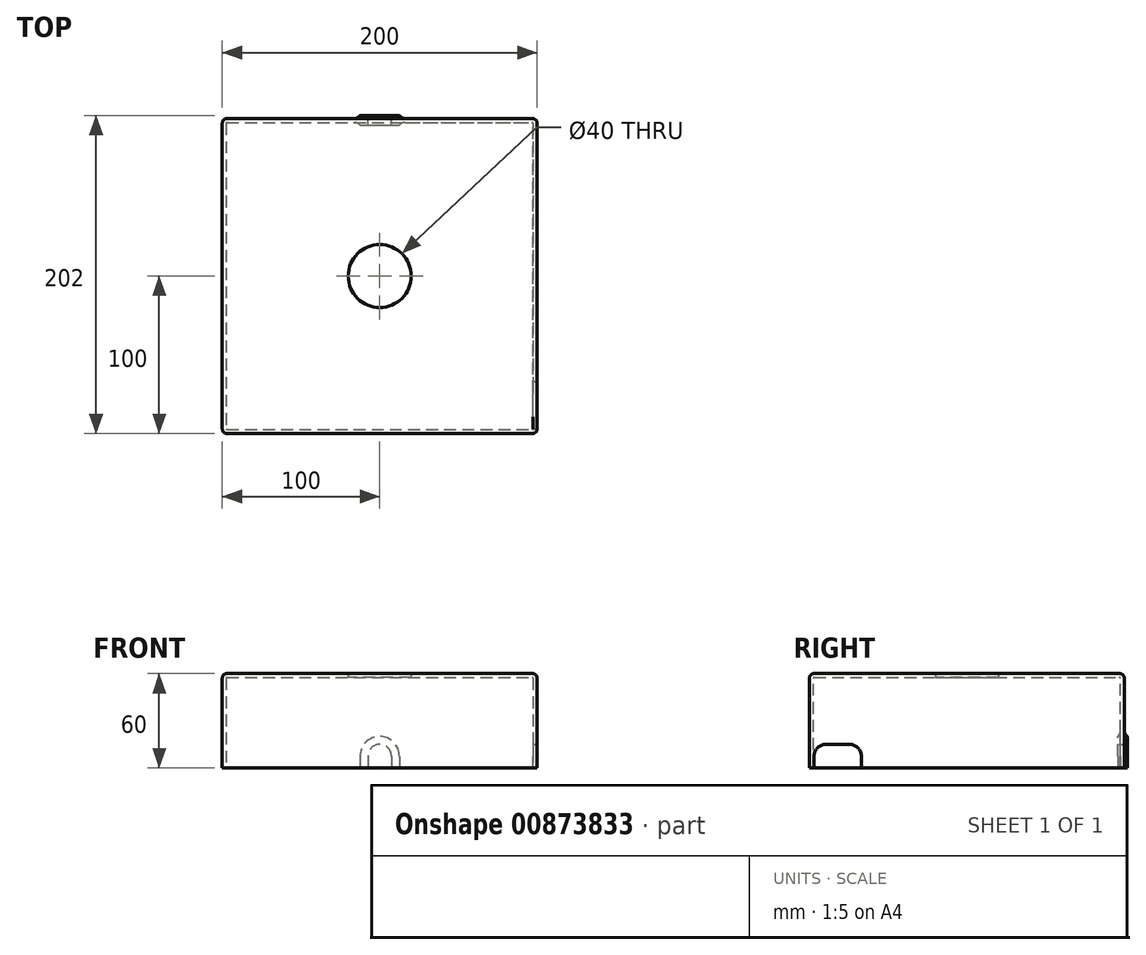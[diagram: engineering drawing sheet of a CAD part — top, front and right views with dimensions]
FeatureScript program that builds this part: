
annotation { "Feature Type Name" : "Feature", "Feature Type Description" : "" }
export const myFeature = defineFeature(function(context is Context, id is Id, definition is map)
    precondition{}
    {
        {
            var Q0;
            Q0=qCreatedBy(makeId("Top.planeOp"),FACE);
            var sketch = newSketch(context, id + "F0", { "sketchPlane" : qUnion([Q0])});
            skLineSegment(sketch, "E0.bottom", {"start": v(0, 0) * mm, "end": v(200, 0) * mm});
            skLineSegment(sketch, "E0.top", {"start": v(0, -200) * mm, "end": v(200, -200) * mm});
            skLineSegment(sketch, "E0.left", {"start": v(0, 0) * mm, "end": v(0, -200) * mm});
            skLineSegment(sketch, "E0.right", {"start": v(200, 0) * mm, "end": v(200, -200) * mm});
            skCircle(sketch, "E1", {"center": v(100, -100) * mm, "radius": 20 * mm});
            skPoint(sketch, "E1.centerSnap0", {"position": v(0, -100) * mm});
            skPoint(sketch, "E1.centerSnap1", {"position": v(100, 0) * mm});
            skSolve(sketch);
        }
        {
            var Q0;
            Q0=makeQuery(id+"F0.imprint","IMPRINT",FACE,{"disambiguationData":[TD([[makeQuery(id+"F0.imprint","IMPRINT",EDGE,{"derivedFrom":sQuery(id+"F0.wireOp",EDGE,"E0.bottom")}),-1.0]])]});
            var Q1;
            Q1=makeQuery(id+"F0.imprint","IMPRINT",FACE,{"disambiguationData":[TD([[makeQuery(id+"F0.imprint","IMPRINT",EDGE,{"derivedFrom":sQuery(id+"F0.wireOp",EDGE,"E1")}),1.0]])]});
            extrude(context, id + "F1", {"entities" : qUnion([Q0, Q1]), "depth" : 60 * mm, "offsetDistance" : 25 * mm});
        }
        {
            var Q0;
            Q0=makeQuery(id+"F1.opExtrude","CAP_EDGE",EDGE,{"disambiguationData":[OSD([sQuery(id+"F0.wireOp",EDGE,"E0.bottom")])],"isStart":false});
            var Q1;
            Q1=makeQuery(id+"F1.opExtrude","CAP_EDGE",EDGE,{"disambiguationData":[OSD([sQuery(id+"F0.wireOp",EDGE,"E0.right")])],"isStart":false});
            var Q2;
            Q2=makeQuery(id+"F1.opExtrude","CAP_EDGE",EDGE,{"disambiguationData":[OSD([sQuery(id+"F0.wireOp",EDGE,"E0.top")])],"isStart":false});
            var Q3;
            Q3=makeQuery(id+"F1.opExtrude","CAP_EDGE",EDGE,{"disambiguationData":[OSD([sQuery(id+"F0.wireOp",EDGE,"E0.left")])],"isStart":false});
            var Q4;
            Q4=makeQuery(id+"F1.opExtrude","SWEPT_EDGE",EDGE,{"disambiguationData":[OSD([sQuery(id+"F0.wireOp",EDGE,"E0.bottom"),sQuery(id+"F0.wireOp",EDGE,"E0.left")])]});
            var Q5;
            Q5=makeQuery(id+"F1.opExtrude","SWEPT_EDGE",EDGE,{"disambiguationData":[OSD([sQuery(id+"F0.wireOp",EDGE,"E0.top"),sQuery(id+"F0.wireOp",EDGE,"E0.left")])]});
            var Q6;
            Q6=makeQuery(id+"F1.opExtrude","SWEPT_EDGE",EDGE,{"disambiguationData":[OSD([sQuery(id+"F0.wireOp",EDGE,"E0.top"),sQuery(id+"F0.wireOp",EDGE,"E0.right")])]});
            var Q7;
            Q7=makeQuery(id+"F1.opExtrude","SWEPT_EDGE",EDGE,{"disambiguationData":[OSD([sQuery(id+"F0.wireOp",EDGE,"E0.bottom"),sQuery(id+"F0.wireOp",EDGE,"E0.right")])]});
            fillet(context, id + "F2", {"entities" : qUnion([Q0, Q1, Q2, Q3, Q4, Q5, Q6, Q7]), "radius" : 3 * mm, "tangentPropagation" : true, "allowEdgeOverflow" : false});
        }
        {
            var Q0;
            Q0=makeQuery(id+"F1.opExtrude","CAP_FACE",FACE,{"disambiguationData":[OSD([sQuery(id+"F0.wireOp",EDGE,"E0.bottom"),sQuery(id+"F0.wireOp",EDGE,"E0.top"),sQuery(id+"F0.wireOp",EDGE,"E0.left"),sQuery(id+"F0.wireOp",EDGE,"E0.right")])],"isStart":true});
            shell(context, id + "F3", {"entities" : qUnion([Q0]), "thickness" : 2.5 * mm});
        }
        {
            var Q0;
            Q0=makeQuery(id+"F0.imprint","IMPRINT",FACE,{"disambiguationData":[TD([[makeQuery(id+"F0.imprint","IMPRINT",EDGE,{"derivedFrom":sQuery(id+"F0.wireOp",EDGE,"E1")}),1.0]])]});
            var Q1;
            Q1=makeQuery(id+"F1.opExtrude","CAP_FACE",FACE,{"disambiguationData":[OSD([sQuery(id+"F0.wireOp",EDGE,"E0.bottom"),sQuery(id+"F0.wireOp",EDGE,"E0.top"),sQuery(id+"F0.wireOp",EDGE,"E0.left"),sQuery(id+"F0.wireOp",EDGE,"E0.right")])],"isStart":false});
            extrude(context, id + "F4", {"entities" : qUnion([Q0]), "operationType" : NewBodyOperationType.REMOVE, "endBound" : BoundingType.UP_TO_SURFACE, "depth" : 25 * mm, "endBoundEntityFace" : qUnion([Q1]), "offsetDistance" : 25 * mm});
        }
        {
            var Q0;
            Q0=makeQuery(id+"F1.opExtrude","SWEPT_FACE",FACE,{"disambiguationData":[OSD([sQuery(id+"F0.wireOp",EDGE,"E0.right")])]});
            var sketch = newSketch(context, id + "F5", { "sketchPlane" : qUnion([Q0])});
            skLineSegment(sketch, "E2.bottom", {"start": v(-197, 0) * mm, "end": v(-167, 0) * mm});
            skLineSegment(sketch, "E2.top", {"start": v(-189.5, 15) * mm, "end": v(-174.5, 15) * mm});
            skLineSegment(sketch, "E2.left", {"start": v(-197, 0) * mm, "end": v(-197, 7.5) * mm});
            skLineSegment(sketch, "E2.right", {"start": v(-167, 0) * mm, "end": v(-167, 7.5) * mm});
            skPoint(sketch, "E3.visualSharp", {"position": v(-197, 15) * mm});
            skArc(sketch, "E3.filletArc", {"start": v(-189.5, 15) * mm, "mid": v(-194.8, 12.8) * mm, "end": v(-197, 7.5) * mm});
            skPoint(sketch, "E4.visualSharp", {"position": v(-167, 15) * mm});
            skArc(sketch, "E4.filletArc", {"start": v(-167, 7.5) * mm, "mid": v(-169.2, 12.8) * mm, "end": v(-174.5, 15) * mm});
            skSolve(sketch);
        }
        {
            var Q0;
            Q0=makeQuery(id+"F5.imprint","IMPRINT",FACE,{"disambiguationData":[TD([[makeQuery(id+"F5.imprint","IMPRINT",EDGE,{"derivedFrom":sQuery(id+"F5.wireOp",EDGE,"E2.bottom")}),-1.0]])]});
            extrude(context, id + "F6", {"entities" : qUnion([Q0]), "operationType" : NewBodyOperationType.REMOVE, "oppositeDirection" : true, "depth" : 25 * mm, "offsetDistance" : 25 * mm});
        }
        {
            var Q0;
            Q0=makeQuery(id+"F1.opExtrude","SWEPT_FACE",FACE,{"disambiguationData":[OSD([sQuery(id+"F0.wireOp",EDGE,"E0.bottom")])]});
            var sketch = newSketch(context, id + "F7", { "sketchPlane" : qUnion([Q0])});
            skArc(sketch, "E5", {"start": v(-92.5, 7.5) * mm, "mid": v(-100, 15) * mm, "end": v(-107.5, 7.5) * mm});
            skPoint(sketch, "E5.centerSnap0", {"position": v(-100, 0) * mm});
            skLineSegment(sketch, "E6", {"start": v(-92.5, 7.5) * mm, "end": v(-92.5, 0) * mm});
            skLineSegment(sketch, "E7", {"start": v(-107.5, 7.5) * mm, "end": v(-107.5, 0) * mm});
            skLineSegment(sketch, "E8.0", {"start": v(-112.5, 7.5) * mm, "end": v(-112.5, 0) * mm});
            skArc(sketch, "E8.1", {"start": v(-87.5, 7.5) * mm, "mid": v(-100, 20) * mm, "end": v(-112.5, 7.5) * mm});
            skLineSegment(sketch, "E8.2", {"start": v(-87.5, 7.5) * mm, "end": v(-87.5, 0) * mm});
            skSolve(sketch);
        }
        {
            var Q0;
            Q0=makeQuery(id+"F7.imprint","IMPRINT",FACE,{"disambiguationData":[TD([[makeQuery(id+"F7.imprint","IMPRINT",EDGE,{"derivedFrom":sQuery(id+"F7.wireOp",EDGE,"E5")}),1.0]])]});
            extrude(context, id + "F8", {"entities" : qUnion([Q0]), "operationType" : NewBodyOperationType.REMOVE, "oppositeDirection" : true, "depth" : 25 * mm, "offsetDistance" : 25 * mm});
        }
        {
            var Q0;
            Q0=makeQuery(id+"F7.imprint","IMPRINT",FACE,{"disambiguationData":[TD([[makeQuery(id+"F7.imprint","IMPRINT",EDGE,{"derivedFrom":sQuery(id+"F7.wireOp",EDGE,"E5")}),-1.0]])]});
            extrude(context, id + "F9", {"entities" : qUnion([Q0]), "operationType" : NewBodyOperationType.ADD, "depth" : 2 * mm, "offsetDistance" : 25 * mm, "hasSecondDirection" : true, "secondDirectionOppositeDirection" : true, "secondDirectionDepth" : 4 * mm});
        }
        {
            var Q0;
            Q0=makeQuery(id+"F9.boolean.opBoolean","INTERSECT",EDGE,{"derivedFrom":[makeQuery(id+"F1.opExtrude","SWEPT_FACE",FACE,{"disambiguationData":[OSD([sQuery(id+"F0.wireOp",EDGE,"E0.bottom")])]}),makeQuery(id+"F9.opExtrude","SWEPT_FACE",FACE,{"disambiguationData":[OSD([sQuery(id+"F7.wireOp",EDGE,"E8.1")])]})]});
            var Q1;
            {var subQ0=sQuery(id+"F0.wireOp",EDGE,"E0.bottom");Q1=makeQuery(id+"F9.boolean.opBoolean","INTERSECT",EDGE,{"derivedFrom":[makeQuery(id+"F3.opShell","OFFSET_FACE",FACE,{"disambiguationData":[OSD([subQ0]),TDD([makeQuery(id+"F1.opExtrude","SWEPT_FACE",FACE,{"disambiguationData":[OSD([subQ0])]})])]}),makeQuery(id+"F9.opExtrude","SWEPT_FACE",FACE,{"disambiguationData":[OSD([sQuery(id+"F7.wireOp",EDGE,"E8.1")])]})]});}
            fillet(context, id + "F10", {"entities" : qUnion([Q0, Q1]), "radius" : 5 * mm, "tangentPropagation" : true, "allowEdgeOverflow" : false});
        }
    });
